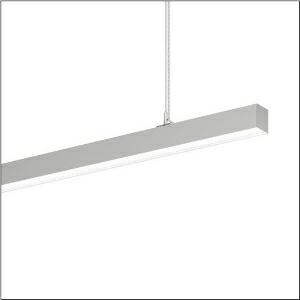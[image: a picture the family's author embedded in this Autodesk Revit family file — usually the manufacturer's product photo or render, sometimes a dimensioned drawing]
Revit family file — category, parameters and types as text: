
# Revit family: silica_r__21_51mx33da37sb_bea4
name_source: partatom
category: Lighting Fixtures
units: mm (PartAtom-declared; Revit-internal decimal feet)

## family parameters
Cut with Voids When Loaded = No
Host = Face
Light Source = No
Part Type = Normal
Room Calculation Point = No
Round Connector Dimension = Use Diameter
Shared = No

## types (1)
- --- (1 x LED, 5910 lm, 41.3 W, 3000K)
    Apparent Load = 41 VA
    CIE Flux Codes = 78 96 99 55 100
    Color Rendering = 80
    Color Temperature = 3000K
    Default Elevation = 1800 mm
    Description = Silica® 21, office luminaire, primary optical cover: prismatic diffuser, of PMMA, CAT 2 (L<= 3000cd/m²), light emission: direct/indirect distribution, primary light characteristic: symmetric, installation type: suspended mounting, LED, rated luminous flux: 5.910lm, luminous efficacy: 143lm/W, light colour: 830, colour temperature: 3000K, control gear: DALI 2, with terminal, 3+2-pole, max. 2.5mm², mains connection: 220..240V, AC, 50/60Hz, rated input power: 41.3W, luminaire housing, of aluminium, metallic grey (RAL 9006), length: 1.204mm, width: 53mm, height: 53mm, protection rating (complete): IP20, insulation class (complete): insulation class I (protective earthing), certification: CE, permissible operating ambient temperature: 0..+35°C, standard: EN 50419, packaging unit: 1 piece
    Height = 53 mm
    Lamp = 1 x LED
    Lamp Light Flux = 5910 lm
    Lamp Power = 41.3 W
    Lamp count = 1
    Length = 1204 mm
    Luminous efficacy = 143 lm/W
    Manufacturer = Siteco
    ModVariant = No
    Model = 51MX33DA37SB
    Mounting Place = Ceiling
    Mounting Type = Pendant
    Number of Poles = 1
    OnlyDefault = Yes
    Power Factor = 1
    Product Name = Silica® 21
    Product group = office luminaire | ceiling pendant
    ProductGroupID = 904
    Protection Class = Protection class I
    Protection Degree = IP 20
    RLX_Detail_Level = 1
    RLX_Emergency_Light_Flux = 0 lm
    RLX_Emergency_Type = 0
    RLX_Emergency_Type_DB = No
    RlxData = <blob elided: 23397 chars, md5=43bb5969>
    Socket = socket
    Standby Power = 0 W
    System Light Flux = 5910 lm
    System Power = 41 W
    Type Comments = factory setting: luminous flux: 100 % | dim-lin: 254 | 345 mA
    Type Image = l_1335864.jpg
    URL = http://relux.com
    VarID = @adj_118546
    Voltage = 0 V
    Weight = 0.00 kg
    Width = 53 mm

## geometry (parser evidence)
native form markers: Blend x4, Sweep x13
no freeform markers — native parametric forms only
